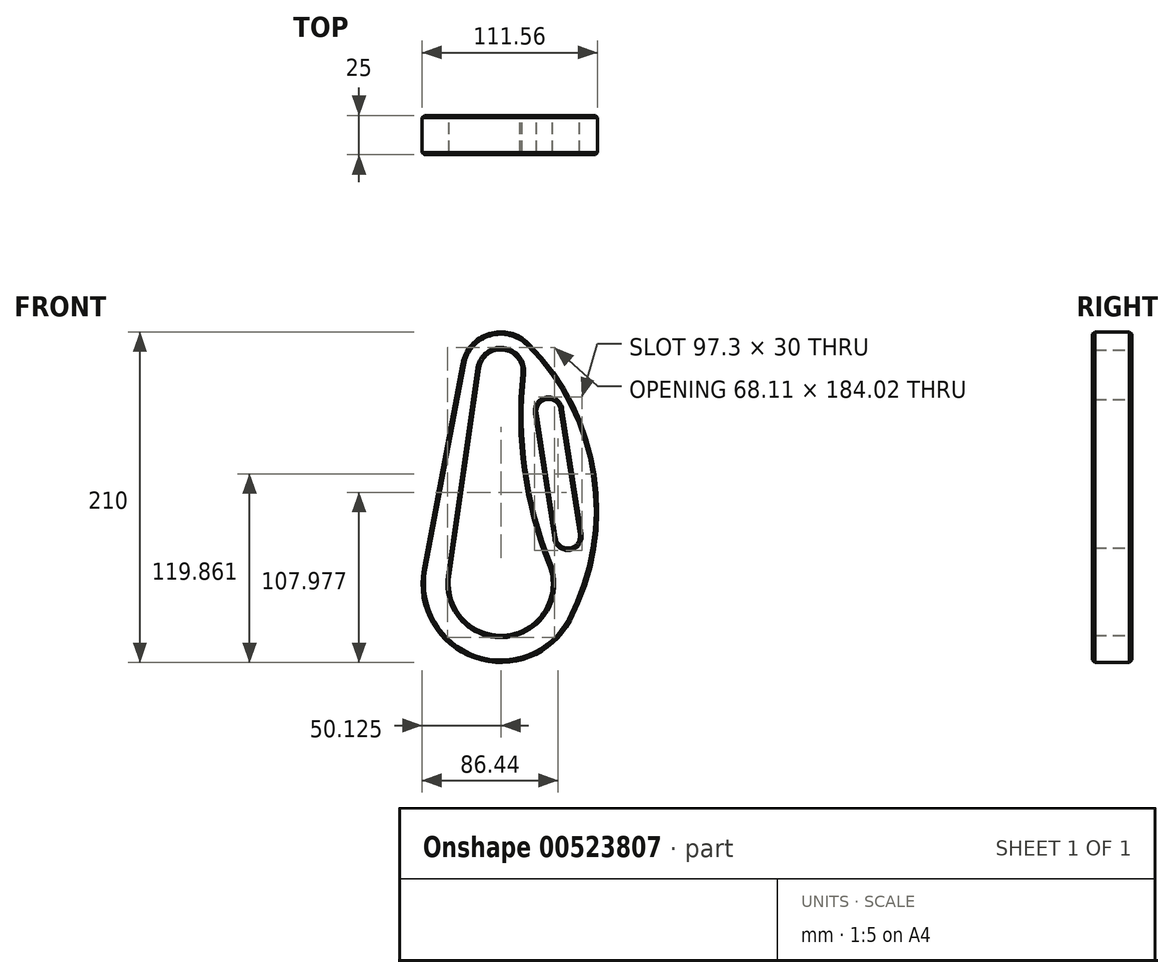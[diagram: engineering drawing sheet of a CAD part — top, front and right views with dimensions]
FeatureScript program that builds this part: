
annotation { "Feature Type Name" : "Feature", "Feature Type Description" : "" }
export const myFeature = defineFeature(function(context is Context, id is Id, definition is map)
    precondition{}
    {
        {
            var Q0;
            Q0=qCreatedBy(makeId("Front.planeOp"),FACE);
            var sketch = newSketch(context, id + "F0", { "sketchPlane" : qUnion([Q0])});
            skArc(sketch, "E0", {"start": v(-49.14, 9.26) * mm, "mid": v(-16.48, -47.2) * mm, "end": v(44.22, -23.33) * mm});
            skArc(sketch, "E1", {"start": v(17.69, 152.67) * mm, "mid": v(-7.37, 158.89) * mm, "end": v(-24.57, 139.63) * mm});
            skLineSegment(sketch, "E2", {"start": v(-24.57, 139.63) * mm, "end": v(-49.14, 9.26) * mm});
            skArc(sketch, "E3", {"start": v(44.22, -23.33) * mm, "mid": v(59.88, 69.03) * mm, "end": v(17.69, 152.67) * mm});
            skArc(sketch, "E4", {"start": v(13.53, 133.55) * mm, "mid": v(1.69, 148.5) * mm, "end": v(-13.47, 136.93) * mm});
            skArc(sketch, "E5", {"start": v(-32.45, 4.66) * mm, "mid": v(3.93, -32.54) * mm, "end": v(30.4, 12.25) * mm});
            skArc(sketch, "E6", {"start": v(13.53, 133.55) * mm, "mid": v(14.5, 71.86) * mm, "end": v(30.4, 12.25) * mm});
            skLineSegment(sketch, "E7", {"start": v(-13.47, 136.93) * mm, "end": v(-32.45, 4.66) * mm});
            skArc(sketch, "E8", {"start": v(37.75, 110.75) * mm, "mid": v(29.2, 117.03) * mm, "end": v(22.93, 108.47) * mm});
            skArc(sketch, "E9", {"start": v(35.13, 28.97) * mm, "mid": v(43.68, 22.7) * mm, "end": v(49.96, 31.25) * mm});
            skLineSegment(sketch, "E10", {"start": v(22.93, 108.47) * mm, "end": v(35.13, 28.97) * mm});
            skLineSegment(sketch, "E11", {"start": v(37.75, 110.75) * mm, "end": v(49.96, 31.25) * mm});
            skSolve(sketch);
        }
        {
            var Q0;
            Q0=makeQuery(id+"F0.imprint","IMPRINT",FACE,{"disambiguationData":[TD([[makeQuery(id+"F0.imprint","IMPRINT",EDGE,{"derivedFrom":sQuery(id+"F0.wireOp",EDGE,"E0")}),1.0]])]});
            extrude(context, id + "F1", {"entities" : qUnion([Q0]), "depth" : 25 * mm, "offsetDistance" : 25 * mm});
        }
        {
            var Q0;
            Q0=makeQuery(id+"F1.opExtrude","CAP_FACE",FACE,{"disambiguationData":[OSD([sQuery(id+"F0.wireOp",EDGE,"E0"),sQuery(id+"F0.wireOp",EDGE,"E1"),sQuery(id+"F0.wireOp",EDGE,"E2"),sQuery(id+"F0.wireOp",EDGE,"E3"),sQuery(id+"F0.wireOp",EDGE,"E4"),sQuery(id+"F0.wireOp",EDGE,"E5"),sQuery(id+"F0.wireOp",EDGE,"E6"),sQuery(id+"F0.wireOp",EDGE,"E7"),sQuery(id+"F0.wireOp",EDGE,"E8"),sQuery(id+"F0.wireOp",EDGE,"E9"),sQuery(id+"F0.wireOp",EDGE,"E10"),sQuery(id+"F0.wireOp",EDGE,"E11")])],"isStart":false});
            var Q1;
            Q1=makeQuery(id+"F1.opExtrude","CAP_FACE",FACE,{"disambiguationData":[OSD([sQuery(id+"F0.wireOp",EDGE,"E0"),sQuery(id+"F0.wireOp",EDGE,"E1"),sQuery(id+"F0.wireOp",EDGE,"E2"),sQuery(id+"F0.wireOp",EDGE,"E3"),sQuery(id+"F0.wireOp",EDGE,"E4"),sQuery(id+"F0.wireOp",EDGE,"E5"),sQuery(id+"F0.wireOp",EDGE,"E6"),sQuery(id+"F0.wireOp",EDGE,"E7"),sQuery(id+"F0.wireOp",EDGE,"E8"),sQuery(id+"F0.wireOp",EDGE,"E9"),sQuery(id+"F0.wireOp",EDGE,"E10"),sQuery(id+"F0.wireOp",EDGE,"E11")])],"isStart":true});
            chamfer(context, id + "F2", {"entities" : qUnion([Q0, Q1]), "width" : 1.5 * mm, "tangentPropagation" : true});
        }
    });
